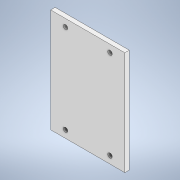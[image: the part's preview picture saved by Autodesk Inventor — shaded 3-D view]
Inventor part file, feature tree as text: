
AUTODESK INVENTOR PART (.ipt)
format: ipt  version: 2021 (Build 250183000, 183)  size: 109,056 bytes
history: native  units: mm
features: extrude x1, sketch x1
ambient origin geometry x8: Origin, YZ Plane, XZ Plane, XY Plane, X Axis, Y Axis, Z Axis, Center Point
bodies: Solid1 (feature_tree)
feature tree (2):
  extrude  "Extrusion1"  Depth=50.0mm
  sketch  "Sketch1"  dims[d0=70.0mm d1=50.0mm d2=3.0mm d3=0.0mm d4=3.0mm d5=3.0mm d6=3.0mm d7=3.0mm d8=5.0mm d9=5.0mm d10=10.0mm d11=10.0mm d12=10.0mm d13=5.0mm d14=10.0mm d15=5.0mm]
